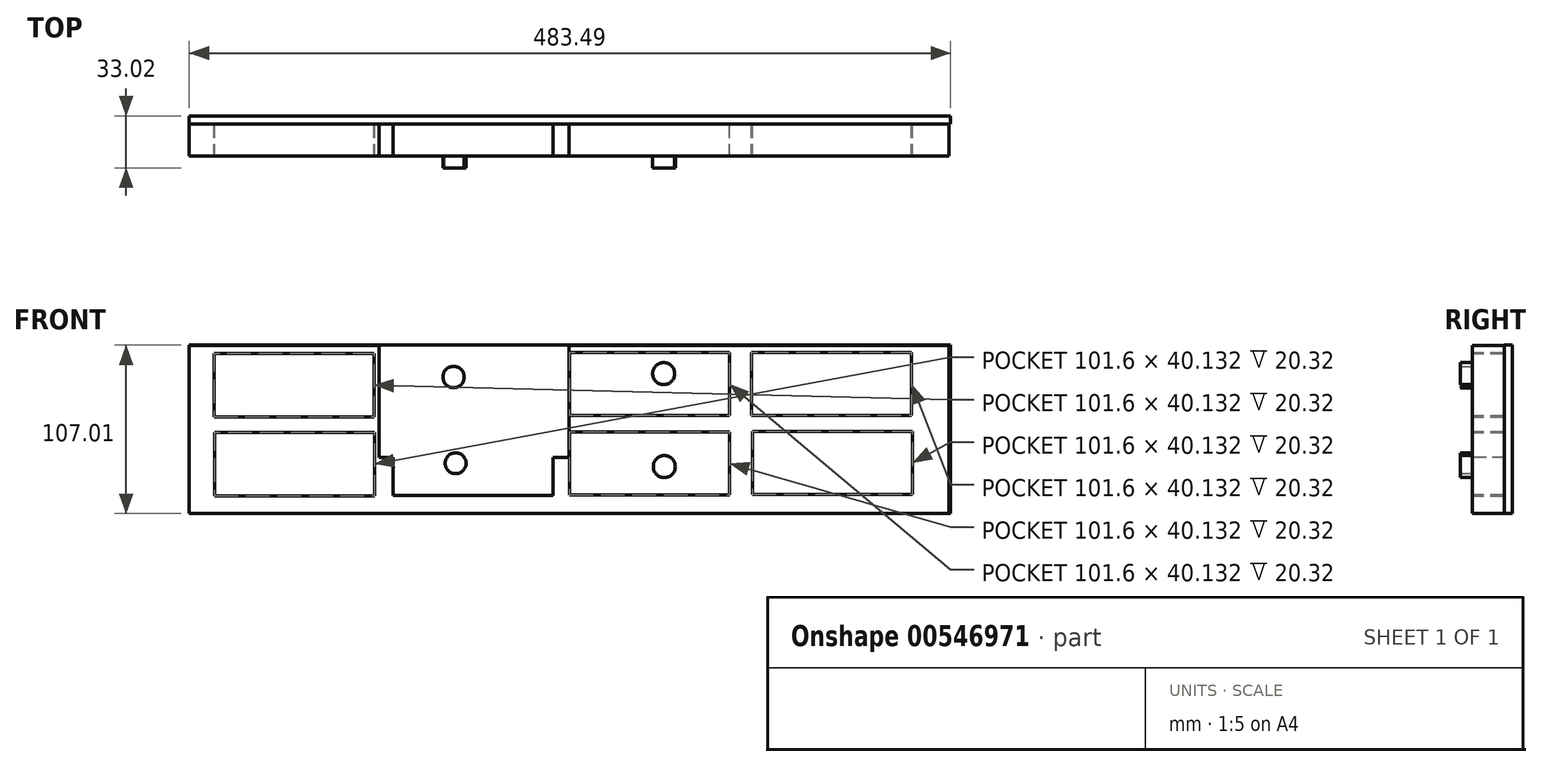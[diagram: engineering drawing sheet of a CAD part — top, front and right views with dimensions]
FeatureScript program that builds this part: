
annotation { "Feature Type Name" : "Feature", "Feature Type Description" : "" }
export const myFeature = defineFeature(function(context is Context, id is Id, definition is map)
    precondition{}
    {
        {
            var Q0;
            Q0=qCreatedBy(makeId("Front.planeOp"),FACE);
            var sketch = newSketch(context, id + "F0", { "sketchPlane" : qUnion([Q0])});
            skLineSegment(sketch, "E0", {"start": v(-271.93, 47.34) * mm, "end": v(210.67, 47.34) * mm});
            skLineSegment(sketch, "E1", {"start": v(210.67, 47.34) * mm, "end": v(210.67, -59.34) * mm});
            skLineSegment(sketch, "E2", {"start": v(210.67, -59.34) * mm, "end": v(-271.93, -59.34) * mm});
            skLineSegment(sketch, "E3", {"start": v(-271.93, -59.34) * mm, "end": v(-271.93, 47.34) * mm});
            skLineSegment(sketch, "E4", {"start": v(-151.28, 47.34) * mm, "end": v(-151.28, -59.34) * mm});
            skLineSegment(sketch, "E5", {"start": v(-30.63, 47.34) * mm, "end": v(-30.63, -59.34) * mm});
            skLineSegment(sketch, "E6", {"start": v(90.02, 47.34) * mm, "end": v(90.02, -59.34) * mm});
            skLineSegment(sketch, "E7", {"start": v(-271.93, 11.78) * mm, "end": v(210.67, 11.78) * mm});
            skLineSegment(sketch, "E8", {"start": v(210.65, -23.78) * mm, "end": v(-271.93, -23.78) * mm});
            skLineSegment(sketch, "E9", {"start": v(-151, 11.78) * mm, "end": v(-30.63, 11.78) * mm});
            skLineSegment(sketch, "E10", {"start": v(-151.44, -23.78) * mm, "end": v(89.76, -23.78) * mm});
            skLineSegment(sketch, "E11", {"start": v(-30.63, 11.78) * mm, "end": v(-30.64, -23.78) * mm});
            skSolve(sketch);
        }
        {
            var Q0;
            {var subQ0=sQuery(id+"F0.wireOp",EDGE,"E3");var subQ1=sQuery(id+"F0.wireOp",EDGE,"E0");var subQ2=makeQuery(id+"F0.imprint","INTERSECT",VERTEX,{"derivedFrom":[subQ1,subQ0]});Q0=makeQuery(id+"F0.imprint","IMPRINT",FACE,{"disambiguationData":[TD([[makeQuery(id+"F0.imprint","IMPRINT",EDGE,{"disambiguationData":[TD([[subQ2,-1.0]])],"derivedFrom":subQ1}),-1.0]])]});}
            var Q1;
            {var subQ0=sQuery(id+"F0.wireOp",EDGE,"E1");var subQ1=sQuery(id+"F0.wireOp",EDGE,"E0");var subQ2=makeQuery(id+"F0.imprint","INTERSECT",VERTEX,{"derivedFrom":[subQ1,subQ0]});Q1=makeQuery(id+"F0.imprint","IMPRINT",FACE,{"disambiguationData":[TD([[makeQuery(id+"F0.imprint","IMPRINT",EDGE,{"disambiguationData":[TD([[subQ2,1.0]])],"derivedFrom":subQ1}),-1.0]])]});}
            var Q2;
            {var subQ0=sQuery(id+"F0.wireOp",EDGE,"E9");Q2=makeQuery(id+"F0.imprint","IMPRINT",FACE,{"disambiguationData":[TD([[makeQuery(id+"F0.imprint","IMPRINT",EDGE,{"derivedFrom":subQ0}),1.0]])]});}
            var Q3;
            {var subQ1=sQuery(id+"F0.wireOp",EDGE,"E3");var subQ5=sQuery(id+"F0.wireOp",EDGE,"E7");var subQ6=makeQuery(id+"F0.imprint","INTERSECT",VERTEX,{"derivedFrom":[subQ1,subQ5]});Q3=makeQuery(id+"F0.imprint","IMPRINT",FACE,{"disambiguationData":[TD([[makeQuery(id+"F0.imprint","IMPRINT",EDGE,{"disambiguationData":[TD([[subQ6,1.0]])],"derivedFrom":subQ1}),-1.0]])]});}
            var Q4;
            {var subQ0=sQuery(id+"F0.wireOp",EDGE,"E5");var subQ1=sQuery(id+"F0.wireOp",EDGE,"E0");var subQ2=makeQuery(id+"F0.imprint","INTERSECT",VERTEX,{"derivedFrom":[subQ1,subQ0]});Q4=makeQuery(id+"F0.imprint","IMPRINT",FACE,{"disambiguationData":[TD([[makeQuery(id+"F0.imprint","IMPRINT",EDGE,{"disambiguationData":[TD([[subQ2,-1.0]])],"derivedFrom":subQ1}),-1.0]])]});}
            var Q5;
            {var subQ1=sQuery(id+"F0.wireOp",EDGE,"E3");var subQ6=sQuery(id+"F0.wireOp",EDGE,"E2");var subQ9=makeQuery(id+"F0.imprint","INTERSECT",VERTEX,{"derivedFrom":[subQ6,subQ1]});Q5=makeQuery(id+"F0.imprint","IMPRINT",FACE,{"disambiguationData":[TD([[makeQuery(id+"F0.imprint","IMPRINT",EDGE,{"disambiguationData":[TD([[subQ9,1.0]])],"derivedFrom":subQ6}),-1.0]])]});}
            var Q6;
            {var subQ1=sQuery(id+"F0.wireOp",EDGE,"E2");var subQ4=sQuery(id+"F0.wireOp",EDGE,"E1");var subQ5=makeQuery(id+"F0.imprint","INTERSECT",VERTEX,{"derivedFrom":[subQ4,subQ1]});Q6=makeQuery(id+"F0.imprint","IMPRINT",FACE,{"disambiguationData":[TD([[makeQuery(id+"F0.imprint","IMPRINT",EDGE,{"disambiguationData":[TD([[subQ5,1.0]])],"derivedFrom":subQ4}),-1.0]])]});}
            var Q7;
            {var subQ5=sQuery(id+"F0.wireOp",EDGE,"E2");var subQ7=sQuery(id+"F0.wireOp",EDGE,"E5");var subQ9=makeQuery(id+"F0.imprint","INTERSECT",VERTEX,{"derivedFrom":[subQ5,subQ7]});Q7=makeQuery(id+"F0.imprint","IMPRINT",FACE,{"disambiguationData":[TD([[makeQuery(id+"F0.imprint","IMPRINT",EDGE,{"disambiguationData":[TD([[subQ9,1.0]])],"derivedFrom":subQ5}),-1.0]])]});}
            var Q8;
            {var subQ2=sQuery(id+"F0.wireOp",EDGE,"E4");var subQ4=sQuery(id+"F0.wireOp",EDGE,"E2");var subQ5=makeQuery(id+"F0.imprint","INTERSECT",VERTEX,{"derivedFrom":[subQ4,subQ2]});Q8=makeQuery(id+"F0.imprint","IMPRINT",FACE,{"disambiguationData":[TD([[makeQuery(id+"F0.imprint","IMPRINT",EDGE,{"disambiguationData":[TD([[subQ5,1.0]])],"derivedFrom":subQ4}),-1.0]])]});}
            var Q9;
            {var subQ4=sQuery(id+"F0.wireOp",EDGE,"E9");Q9=makeQuery(id+"F0.imprint","IMPRINT",FACE,{"disambiguationData":[TD([[makeQuery(id+"F0.imprint","IMPRINT",EDGE,{"derivedFrom":subQ4}),-1.0]])]});}
            var Q10;
            {var subQ1=sQuery(id+"F0.wireOp",EDGE,"E8");var subQ3=sQuery(id+"F0.wireOp",EDGE,"E6");var subQ4=makeQuery(id+"F0.imprint","INTERSECT",VERTEX,{"derivedFrom":[subQ3,subQ1]});Q10=makeQuery(id+"F0.imprint","IMPRINT",FACE,{"disambiguationData":[TD([[makeQuery(id+"F0.imprint","IMPRINT",EDGE,{"disambiguationData":[TD([[subQ4,1.0]])],"derivedFrom":subQ3}),-1.0]])]});}
            var Q11;
            {var subQ0=sQuery(id+"F0.wireOp",EDGE,"E11");Q11=makeQuery(id+"F0.imprint","IMPRINT",FACE,{"disambiguationData":[TD([[makeQuery(id+"F0.imprint","IMPRINT",EDGE,{"derivedFrom":subQ0}),1.0]])]});}
            extrude(context, id + "F1", {"entities" : qUnion([Q0, Q1, Q2, Q3, Q4, Q5, Q6, Q7, Q8, Q9, Q10, Q11]), "depth" : 25.4 * mm, "offsetDistance" : 25.4 * mm});
        }
        {
            var Q0;
            Q0=qCreatedBy(makeId("Front.planeOp"),FACE);
            var sketch = newSketch(context, id + "F2", { "sketchPlane" : qUnion([Q0])});
            skCircle(sketch, "E12", {"center": v(-103.64, 26.63) * mm, "radius": 10.18 * mm});
            skCircle(sketch, "E13", {"center": v(-103.2, -27.7) * mm, "radius": 10.33 * mm});
            skCircle(sketch, "E14", {"center": v(28.91, 29.23) * mm, "radius": 9.4 * mm});
            skCircle(sketch, "E15", {"center": v(28.91, -29.87) * mm, "radius": 9.33 * mm});
            skArc(sketch, "E16", {"start": v(-106.2, -17.81) * mm, "mid": v(-106.74, -37.4) * mm, "end": v(-94.54, -22.07) * mm});
            skArc(sketch, "E17", {"start": v(-94.54, -22.07) * mm, "mid": v(-113.53, -27.7) * mm, "end": v(-94.54, -33.33) * mm});
            skSolve(sketch);
        }
        {
            var Q0;
            Q0=sQuery(id+"F2.wireOp",VERTEX,"E12.center");
            var Q1;
            Q1=sQuery(id+"F2.wireOp",VERTEX,"E13.center");
            var Q2;
            Q2=sQuery(id+"F2.wireOp",VERTEX,"E14.center");
            var Q3;
            Q3=sQuery(id+"F2.wireOp",VERTEX,"E15.center");
            var Q4;
            Q4=makeQuery(id+"F1.opExtrude","SWEPT_BODY",BODY,{"disambiguationData":[OSD([sQuery(id+"F0.wireOp",EDGE,"E0"),sQuery(id+"F0.wireOp",EDGE,"E1"),sQuery(id+"F0.wireOp",EDGE,"E2"),sQuery(id+"F0.wireOp",EDGE,"E3")])]});
            hole(context, id + "F3", {"style" : HoleStyle.SIMPLE, "endStyle" : HoleEndStyle.THROUGH, "oppositeDirection" : true, "holeDiameter" : 25.4 * mm, "isTappedThrough" : true, "tappedDepth" : 12.7 * mm, "tapClearance" : 3, "locations" : qUnion([Q0, Q1, Q2, Q3]), "scope" : qUnion([Q4])});
        }
        {
            var Q0;
            Q0=qCreatedBy(makeId("Front.planeOp"),FACE);
            var sketch = newSketch(context, id + "F4", { "sketchPlane" : qUnion([Q0])});
            skCircle(sketch, "E18", {"center": v(-104.07, 27.25) * mm, "radius": 6.8 * mm});
            skCircle(sketch, "E19", {"center": v(-102.77, -27.5) * mm, "radius": 6.63 * mm});
            skCircle(sketch, "E20", {"center": v(29.35, 29.42) * mm, "radius": 7 * mm});
            skCircle(sketch, "E21", {"center": v(29.78, -29.68) * mm, "radius": 7 * mm});
            skSolve(sketch);
        }
        {
            var Q0;
            Q0 = qSketchRegion(id + "F4", true);
            extrude(context, id + "F5", {"entities" : qUnion([Q0]), "depth" : 33.02 * mm, "offsetDistance" : 25.4 * mm});
        }
        {
            var Q0;
            Q0=qCreatedBy(makeId("Front.planeOp"),FACE);
            var sketch = newSketch(context, id + "F6", { "sketchPlane" : qUnion([Q0])});
            skLineSegment(sketch, "E22.bottom", {"start": v(-143.1, 42.43) * mm, "end": v(-41.5, 42.43) * mm});
            skLineSegment(sketch, "E22.top", {"start": v(-143.1, 2.3) * mm, "end": v(-41.5, 2.3) * mm});
            skLineSegment(sketch, "E22.left", {"start": v(-143.1, 42.43) * mm, "end": v(-143.1, 2.3) * mm});
            skLineSegment(sketch, "E22.right", {"start": v(-41.5, 42.43) * mm, "end": v(-41.5, 2.3) * mm});
            skLineSegment(sketch, "E23.bottom", {"start": v(-142.55, -7.75) * mm, "end": v(-40.95, -7.75) * mm});
            skLineSegment(sketch, "E23.top", {"start": v(-142.55, -47.89) * mm, "end": v(-40.95, -47.89) * mm});
            skLineSegment(sketch, "E23.left", {"start": v(-142.55, -7.75) * mm, "end": v(-142.55, -47.89) * mm});
            skLineSegment(sketch, "E23.right", {"start": v(-40.95, -7.75) * mm, "end": v(-40.95, -47.89) * mm});
            skLineSegment(sketch, "E24.bottom", {"start": v(-30.41, 42.95) * mm, "end": v(71.19, 42.95) * mm});
            skLineSegment(sketch, "E24.top", {"start": v(-30.41, 2.82) * mm, "end": v(71.19, 2.82) * mm});
            skLineSegment(sketch, "E24.left", {"start": v(-30.41, 42.95) * mm, "end": v(-30.41, 2.82) * mm});
            skLineSegment(sketch, "E24.right", {"start": v(71.19, 42.95) * mm, "end": v(71.19, 2.82) * mm});
            skLineSegment(sketch, "E25.bottom", {"start": v(-30.41, -7.5) * mm, "end": v(71.19, -7.5) * mm});
            skLineSegment(sketch, "E25.top", {"start": v(-30.41, -47.63) * mm, "end": v(71.19, -47.63) * mm});
            skLineSegment(sketch, "E25.left", {"start": v(-30.41, -7.5) * mm, "end": v(-30.41, -47.63) * mm});
            skLineSegment(sketch, "E25.right", {"start": v(71.19, -7.5) * mm, "end": v(71.19, -47.63) * mm});
            skLineSegment(sketch, "E26.bottom", {"start": v(85.3, 42.85) * mm, "end": v(186.9, 42.85) * mm});
            skLineSegment(sketch, "E26.top", {"start": v(85.3, 2.72) * mm, "end": v(186.9, 2.72) * mm});
            skLineSegment(sketch, "E26.left", {"start": v(85.3, 42.85) * mm, "end": v(85.3, 2.72) * mm});
            skLineSegment(sketch, "E26.right", {"start": v(186.9, 42.85) * mm, "end": v(186.9, 2.72) * mm});
            skLineSegment(sketch, "E27.bottom", {"start": v(85.85, -7.34) * mm, "end": v(187.45, -7.34) * mm});
            skLineSegment(sketch, "E27.top", {"start": v(85.85, -47.47) * mm, "end": v(187.45, -47.47) * mm});
            skLineSegment(sketch, "E27.left", {"start": v(85.85, -7.34) * mm, "end": v(85.85, -47.47) * mm});
            skLineSegment(sketch, "E27.right", {"start": v(187.45, -7.34) * mm, "end": v(187.45, -47.47) * mm});
            skLineSegment(sketch, "E28.bottom", {"start": v(-256.3, 42.15) * mm, "end": v(-154.7, 42.15) * mm});
            skLineSegment(sketch, "E28.top", {"start": v(-256.3, 2.02) * mm, "end": v(-154.7, 2.02) * mm});
            skLineSegment(sketch, "E28.left", {"start": v(-256.3, 42.15) * mm, "end": v(-256.3, 2.02) * mm});
            skLineSegment(sketch, "E28.right", {"start": v(-154.7, 42.15) * mm, "end": v(-154.7, 2.02) * mm});
            skLineSegment(sketch, "E29.bottom", {"start": v(-255.76, -8.04) * mm, "end": v(-154.16, -8.04) * mm});
            skLineSegment(sketch, "E29.top", {"start": v(-255.76, -48.17) * mm, "end": v(-154.16, -48.17) * mm});
            skLineSegment(sketch, "E29.left", {"start": v(-255.76, -8.04) * mm, "end": v(-255.76, -48.17) * mm});
            skLineSegment(sketch, "E29.right", {"start": v(-154.16, -8.04) * mm, "end": v(-154.16, -48.17) * mm});
            skSolve(sketch);
        }
        {
            var Q0;
            Q0 = qSketchRegion(id + "F6", true);
            extrude(context, id + "F7", {"entities" : qUnion([Q0]), "operationType" : NewBodyOperationType.REMOVE, "depth" : 25.4 * mm, "offsetDistance" : 25.4 * mm});
        }
        {
            var Q0;
            Q0=qCreatedBy(makeId("Front.planeOp"),FACE);
            var sketch = newSketch(context, id + "F8", { "sketchPlane" : qUnion([Q0])});
            skLineSegment(sketch, "E30.bottom", {"start": v(-271.98, -59.46) * mm, "end": v(211.5, -59.46) * mm});
            skLineSegment(sketch, "E30.top", {"start": v(-271.98, 47.55) * mm, "end": v(211.5, 47.55) * mm});
            skLineSegment(sketch, "E30.left", {"start": v(-271.98, -59.46) * mm, "end": v(-271.98, 47.55) * mm});
            skLineSegment(sketch, "E30.right", {"start": v(211.5, -59.46) * mm, "end": v(211.5, 47.55) * mm});
            skSolve(sketch);
        }
        {
            var Q0;
            Q0 = qSketchRegion(id + "F8", true);
            extrude(context, id + "F9", {"entities" : qUnion([Q0]), "operationType" : NewBodyOperationType.ADD, "depth" : 5.08 * mm, "offsetDistance" : 25.4 * mm});
        }
    });
